# Revit family: RUFO2 360xWSxH0250xx
name_source: partatom
category: Leuchten
units: mm (PartAtom-declared; Revit-internal decimal feet)

## family parameters
Basisbauteil = Fläche
Beim Laden mit Abzugskörper schneiden = Nein
Bemaßung runder Anschluss = Durchmesser verwenden
Gemeinsam genutzt = Nein
Lichtquelle = Ja
OmniClass-Nummer = 23.80.70.11
OmniClass-Titel = Luminaries for Internal Lighting
Raumberechnungspunkt = Nein
Teiletyp = Normal

## types (18) — shared parameters
Baugruppenkennzeichen = D5020200
Datei für fotometrisches Netz = RUFO2_360.IES
Emissionsform beim Rendern sichtbar = Nein
Farbfilter = 16777215
Farbtemperaturverschiebung bei Dämpfen der Lampe = <Keine Auswahl>
Hersteller = RIDI Leuchten GmbH
Lampe = LED
Neigungswinkel = 90.00°
URL = www.ridi.de
Von Kreisdurchmesser aussenden = 360 mm  [stored 1.1811 ft]
brand = RIDI
conformity mark = CE
electrical safety class = 1
height = 95 mm
ingress protection (IP) code = IP40
length = 360 mm  [stored 1.1811 ft]
nominal frequency = 50-60Hz
nominal voltage = 230
voltage type (AC, DC, UC) = AC
width = 360 mm  [stored 1.1811 ft]
zero-valued in all types: Vorgabe-Ansicht

## per-type parameters (varying)
| type | Modell | Scheinlast | product name | rated input power | weight |
| RUFO2 360NDWS840H0250 | 0420843 | 20 VA | RUFO2 360NDWS840H0250 | 20 | 1,06 kg |
| RUFO2 360NDWS840H0250-RS | 0420843//396 | 20 VA | RUFO2 360NDWS840H0250 | 20 | 1,1 kg |
| RUFO2 360NDWS830H0250 | 0420849 | 20 VA | RUFO2 360NDWS830H0250 | 20 | 1,06 kg |
| RUFO2 360NDWS830H0250-RS | 0420849//396 | 20 VA | RUFO2 360NDWS830H0250-RS | 20 | 1,1 kg |
| RUFO2 360NDWS840H0250-IK | 0420855 | 20 VA | RUFO2 360NDWS840H0250-IK | 20 | 1,06 kg |
| RUFO2 360NDWS840H0250-IK-EDS3 | 0420855//377 | 20 VA | RUFO2 360NDWS840H0250-IK-EDS3 | 20 | 1,26 kg |
| RUFO2 360NDWS840H0250-IK-RS | 0420855//396 | 20 VA | RUFO2 360NDWS840H0250-IK-RS | 20 | 1,1 kg |
| RUFO2 360NDWS830H0250-IK | 0420861 | 20 VA | RUFO2 360NDWS830H0250-IK | 20 | 1,06 kg |
| RUFO2 360NDWS830H0250-IK-EDS3 | 0420861//377 | 20 VA | RUFO2 360NDWS830H0250-IK-EDS3 | 20 | 1,26 kg |
| RUFO2 360NDWS830H0250-IK-RS | 0420861//396 | 20 VA | RUFO2 360NDWS830H0250-IK-RS | 20 | 1,1 kg |
| RUFO2 360DAWS840H0250 | 0430843 | 20 VA | RUFO2 360DAWS840H0250 | 20 | 1,06 kg |
| RUFO2 360DAWS830H0250 | 0430849 | 20 VA | RUFO2 360DAWS830H0250 | 20 | 1,06 kg |
| RUFO2 360DAWS840H0250-IK | 0430855 | 20 VA | RUFO2 360DAWS840H0250-IK | 20 | 1,06 kg |
| RUFO2 360DAWS830H0250-IK | 0430861 | 20 VA | RUFO2 360DAWS830H0250-IK | 20 | 1,06 kg |
| RUFO2 360NDWS840H0250-2K | 0420844 | 18 VA | RUFO2 360NDWS840H0250-2K | 18 | 1,1 kg |
| RUFO2 360NDWS830H0250-2K | 0420850 | 18 VA | RUFO2 360NDWS830H0250-2K | 18 | 1,1 kg |
| RUFO2 360NDWS840H0250-IK-2K | 0420856 | 18 VA | RUFO2 360NDWS840H0250-IK-2K | 18 | 1,1 kg |
| RUFO2 360NDWS830H0250-IK-2K | 0420862 | 18 VA | RUFO2 360NDWS830H0250-IK-2K | 18 | 1,1 kg |

note: [stored X ft] marks values corroborated as IEEE doubles in the binary element streams (Revit-internal decimal feet)
